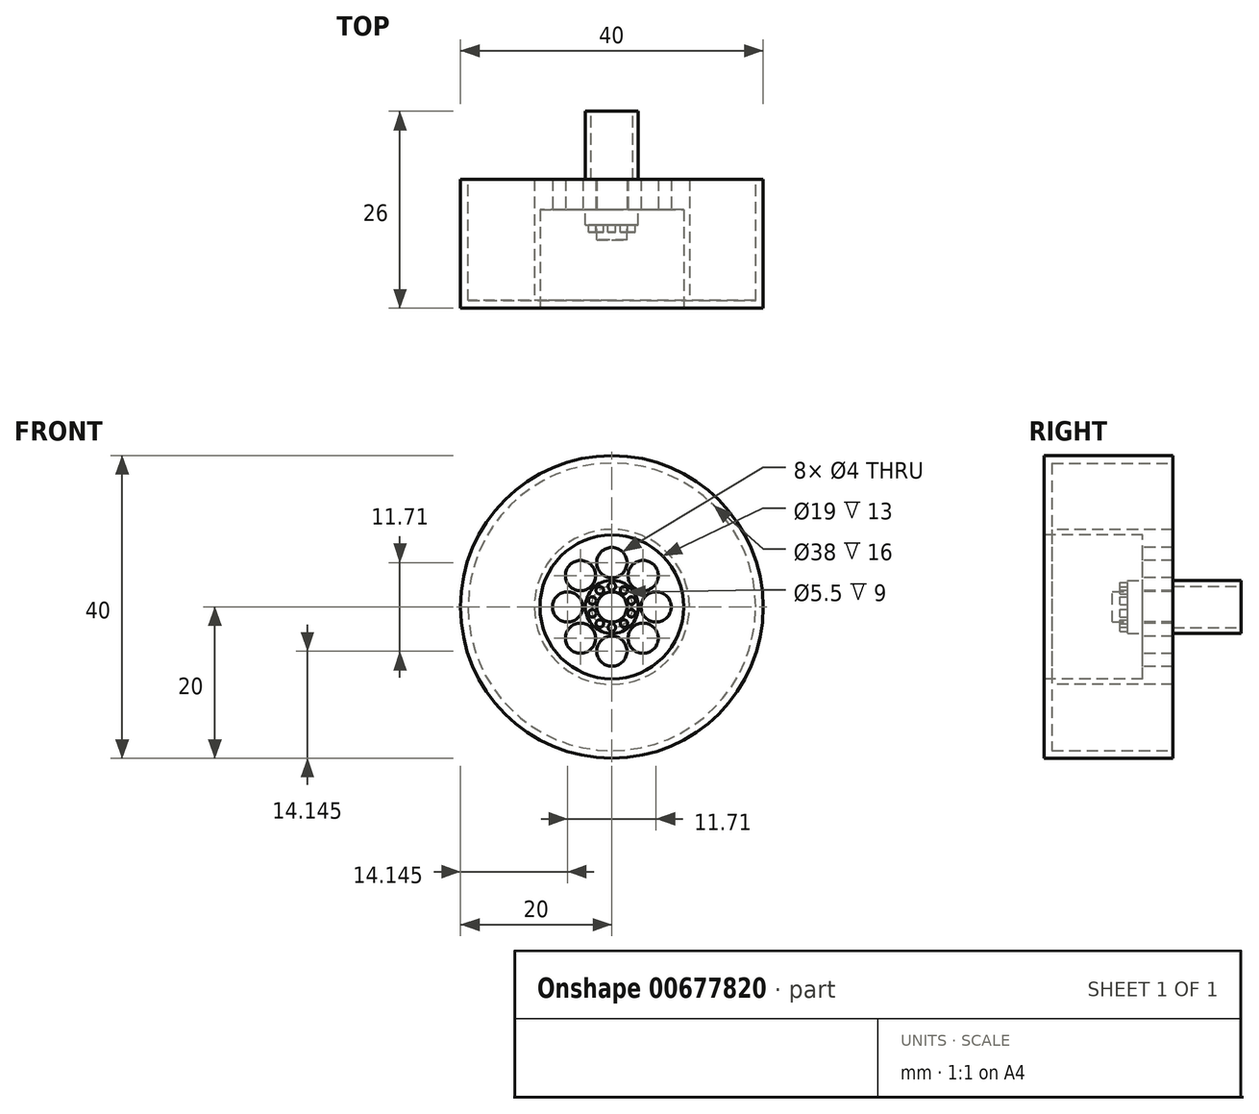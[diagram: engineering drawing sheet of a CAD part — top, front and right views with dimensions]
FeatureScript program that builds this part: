
annotation { "Feature Type Name" : "Feature", "Feature Type Description" : "" }
export const myFeature = defineFeature(function(context is Context, id is Id, definition is map)
    precondition{}
    {
        {
            var Q0;
            Q0=qCreatedBy(makeId("Front.planeOp"),FACE);
            var sketch = newSketch(context, id + "F0", { "sketchPlane" : qUnion([Q0])});
            skCircle(sketch, "E0", {"center": v(0, 0) * mm, "radius": 20 * mm});
            skSolve(sketch);
        }
        {
            var Q0;
            Q0=makeQuery(id+"F0.imprint","IMPRINT",FACE,{"disambiguationData":[TD([[makeQuery(id+"F0.imprint","IMPRINT",EDGE,{"derivedFrom":sQuery(id+"F0.wireOp",EDGE,"E0")}),1.0]])]});
            extrude(context, id + "F1", {"entities" : qUnion([Q0]), "depth" : 17 * mm, "offsetDistance" : 25 * mm});
        }
        {
            var Q0;
            Q0=makeQuery(id+"F1.opExtrude","CAP_FACE",FACE,{"disambiguationData":[OSD([sQuery(id+"F0.wireOp",EDGE,"E0")])],"isStart":false});
            var sketch = newSketch(context, id + "F2", { "sketchPlane" : qUnion([Q0])});
            skCircle(sketch, "E1", {"center": v(0, 0) * mm, "radius": 9.5 * mm});
            skSolve(sketch);
        }
        {
            var Q0;
            Q0=makeQuery(id+"F2.imprint","IMPRINT",FACE,{"disambiguationData":[TD([[makeQuery(id+"F2.imprint","IMPRINT",EDGE,{"derivedFrom":sQuery(id+"F2.wireOp",EDGE,"E1")}),1.0]])]});
            var Q1;
            Q1 = qSketchRegion(id + "F6", true);
            extrude(context, id + "F3", {"entities" : qUnion([Q0, Q1]), "operationType" : NewBodyOperationType.REMOVE, "oppositeDirection" : true, "depth" : 13 * mm, "offsetDistance" : 25 * mm});
        }
        {
            var Q0;
            Q0=makeQuery(id+"F3.boolean.opBoolean","COPY",FACE,{"derivedFrom":makeQuery(id+"F3.opExtrude","CAP_FACE",FACE,{"disambiguationData":[OSD([sQuery(id+"F2.wireOp",EDGE,"E1")])],"isStart":false})});
            var sketch = newSketch(context, id + "F4", { "sketchPlane" : qUnion([Q0])});
            skCircle(sketch, "E2", {"center": v(0, 5.86) * mm, "radius": 2 * mm});
            skCircle(sketch, "E3.1.0", {"center": v(-4.14, 4.14) * mm, "radius": 2 * mm});
            skCircle(sketch, "E3.2.0", {"center": v(-5.86, 0) * mm, "radius": 2 * mm});
            skCircle(sketch, "E3.3.0", {"center": v(-4.14, -4.14) * mm, "radius": 2 * mm});
            skCircle(sketch, "E3.4.0", {"center": v(0, -5.86) * mm, "radius": 2 * mm});
            skCircle(sketch, "E3.5.0", {"center": v(4.14, -4.14) * mm, "radius": 2 * mm});
            skCircle(sketch, "E3.6.0", {"center": v(5.86, 0) * mm, "radius": 2 * mm});
            skCircle(sketch, "E3.7.0", {"center": v(4.14, 4.14) * mm, "radius": 2 * mm});
            skPoint(sketch, "E3.center", {"position": v(0, 0) * mm});
            skSolve(sketch);
        }
        {
            var Q0;
            Q0=makeQuery(id+"F4.imprint","IMPRINT",FACE,{"disambiguationData":[TD([[makeQuery(id+"F4.imprint","IMPRINT",EDGE,{"derivedFrom":sQuery(id+"F4.wireOp",EDGE,"E3.1.0")}),1.0]])]});
            var Q1;
            Q1=makeQuery(id+"F4.imprint","IMPRINT",FACE,{"disambiguationData":[TD([[makeQuery(id+"F4.imprint","IMPRINT",EDGE,{"derivedFrom":sQuery(id+"F4.wireOp",EDGE,"E2")}),1.0]])]});
            var Q2;
            Q2=makeQuery(id+"F4.imprint","IMPRINT",FACE,{"disambiguationData":[TD([[makeQuery(id+"F4.imprint","IMPRINT",EDGE,{"derivedFrom":sQuery(id+"F4.wireOp",EDGE,"E3.7.0")}),1.0]])]});
            var Q3;
            Q3=makeQuery(id+"F4.imprint","IMPRINT",FACE,{"disambiguationData":[TD([[makeQuery(id+"F4.imprint","IMPRINT",EDGE,{"derivedFrom":sQuery(id+"F4.wireOp",EDGE,"E3.6.0")}),1.0]])]});
            var Q4;
            Q4=makeQuery(id+"F4.imprint","IMPRINT",FACE,{"disambiguationData":[TD([[makeQuery(id+"F4.imprint","IMPRINT",EDGE,{"derivedFrom":sQuery(id+"F4.wireOp",EDGE,"E3.5.0")}),1.0]])]});
            var Q5;
            Q5=makeQuery(id+"F4.imprint","IMPRINT",FACE,{"disambiguationData":[TD([[makeQuery(id+"F4.imprint","IMPRINT",EDGE,{"derivedFrom":sQuery(id+"F4.wireOp",EDGE,"E3.4.0")}),1.0]])]});
            var Q6;
            Q6=makeQuery(id+"F4.imprint","IMPRINT",FACE,{"disambiguationData":[TD([[makeQuery(id+"F4.imprint","IMPRINT",EDGE,{"derivedFrom":sQuery(id+"F4.wireOp",EDGE,"E3.3.0")}),1.0]])]});
            var Q7;
            Q7=makeQuery(id+"F4.imprint","IMPRINT",FACE,{"disambiguationData":[TD([[makeQuery(id+"F4.imprint","IMPRINT",EDGE,{"derivedFrom":sQuery(id+"F4.wireOp",EDGE,"E3.2.0")}),1.0]])]});
            extrude(context, id + "F5", {"entities" : qUnion([Q0, Q1, Q2, Q3, Q4, Q5, Q6, Q7]), "operationType" : NewBodyOperationType.REMOVE, "oppositeDirection" : true, "depth" : 4 * mm, "offsetDistance" : 25 * mm});
        }
        {
            var Q0;
            Q0=makeQuery(id+"F3.boolean.opBoolean","COPY",FACE,{"derivedFrom":makeQuery(id+"F3.opExtrude","CAP_FACE",FACE,{"disambiguationData":[OSD([sQuery(id+"F2.wireOp",EDGE,"E1")])],"isStart":false})});
            var sketch = newSketch(context, id + "F6", { "sketchPlane" : qUnion([Q0])});
            skCircle(sketch, "E4", {"center": v(0, 0) * mm, "radius": 3.5 * mm});
            skSolve(sketch);
        }
        {
            var Q0;
            Q0=makeQuery(id+"F6.imprint","IMPRINT",FACE,{"disambiguationData":[TD([[makeQuery(id+"F6.imprint","IMPRINT",EDGE,{"derivedFrom":sQuery(id+"F6.wireOp",EDGE,"E4")}),1.0]])]});
            extrude(context, id + "F7", {"entities" : qUnion([Q0]), "operationType" : NewBodyOperationType.ADD, "depth" : 2 * mm, "offsetDistance" : 25 * mm});
        }
        {
            var Q0;
            Q0=makeQuery(id+"F7.opExtrude","CAP_FACE",FACE,{"disambiguationData":[OSD([sQuery(id+"F6.wireOp",EDGE,"E4")])],"isStart":false});
            var sketch = newSketch(context, id + "F8", { "sketchPlane" : qUnion([Q0])});
            skCircle(sketch, "E5", {"center": v(0, 0) * mm, "radius": 2 * mm});
            skSolve(sketch);
        }
        {
            var Q0;
            Q0=makeQuery(id+"F8.imprint","IMPRINT",FACE,{"disambiguationData":[TD([[makeQuery(id+"F8.imprint","IMPRINT",EDGE,{"derivedFrom":sQuery(id+"F8.wireOp",EDGE,"E5")}),1.0]])]});
            extrude(context, id + "F9", {"entities" : qUnion([Q0]), "operationType" : NewBodyOperationType.ADD, "depth" : 2 * mm, "offsetDistance" : 25 * mm});
        }
        {
            var Q0;
            Q0=makeQuery(id+"F7.opExtrude","CAP_FACE",FACE,{"disambiguationData":[OSD([sQuery(id+"F6.wireOp",EDGE,"E4")])],"isStart":false});
            var sketch = newSketch(context, id + "F10", { "sketchPlane" : qUnion([Q0])});
            skCircle(sketch, "E6", {"center": v(0, 2.71) * mm, "radius": 0.5 * mm});
            skCircle(sketch, "E7.1.0", {"center": v(-1.6, 2.2) * mm, "radius": 0.5 * mm});
            skCircle(sketch, "E7.2.0", {"center": v(-2.58, 0.84) * mm, "radius": 0.5 * mm});
            skCircle(sketch, "E7.3.0", {"center": v(-2.58, -0.84) * mm, "radius": 0.5 * mm});
            skCircle(sketch, "E7.4.0", {"center": v(-1.6, -2.2) * mm, "radius": 0.5 * mm});
            skCircle(sketch, "E7.5.0", {"center": v(0, -2.71) * mm, "radius": 0.5 * mm});
            skCircle(sketch, "E7.6.0", {"center": v(1.6, -2.2) * mm, "radius": 0.5 * mm});
            skCircle(sketch, "E7.7.0", {"center": v(2.58, -0.84) * mm, "radius": 0.5 * mm});
            skCircle(sketch, "E7.8.0", {"center": v(2.58, 0.84) * mm, "radius": 0.5 * mm});
            skCircle(sketch, "E7.9.0", {"center": v(1.6, 2.2) * mm, "radius": 0.5 * mm});
            skPoint(sketch, "E7.center", {"position": v(0, 0) * mm});
            skSolve(sketch);
        }
        {
            var Q0;
            Q0=makeQuery(id+"F10.imprint","IMPRINT",FACE,{"disambiguationData":[TD([[makeQuery(id+"F10.imprint","IMPRINT",EDGE,{"derivedFrom":sQuery(id+"F10.wireOp",EDGE,"E6")}),1.0]])]});
            var Q1;
            Q1=makeQuery(id+"F10.imprint","IMPRINT",FACE,{"disambiguationData":[TD([[makeQuery(id+"F10.imprint","IMPRINT",EDGE,{"derivedFrom":sQuery(id+"F10.wireOp",EDGE,"E7.9.0")}),1.0]])]});
            var Q2;
            Q2=makeQuery(id+"F10.imprint","IMPRINT",FACE,{"disambiguationData":[TD([[makeQuery(id+"F10.imprint","IMPRINT",EDGE,{"derivedFrom":sQuery(id+"F10.wireOp",EDGE,"E7.8.0")}),1.0]])]});
            var Q3;
            Q3=makeQuery(id+"F10.imprint","IMPRINT",FACE,{"disambiguationData":[TD([[makeQuery(id+"F10.imprint","IMPRINT",EDGE,{"derivedFrom":sQuery(id+"F10.wireOp",EDGE,"E7.7.0")}),1.0]])]});
            var Q4;
            Q4=makeQuery(id+"F10.imprint","IMPRINT",FACE,{"disambiguationData":[TD([[makeQuery(id+"F10.imprint","IMPRINT",EDGE,{"derivedFrom":sQuery(id+"F10.wireOp",EDGE,"E7.6.0")}),1.0]])]});
            var Q5;
            Q5=makeQuery(id+"F10.imprint","IMPRINT",FACE,{"disambiguationData":[TD([[makeQuery(id+"F10.imprint","IMPRINT",EDGE,{"derivedFrom":sQuery(id+"F10.wireOp",EDGE,"E7.5.0")}),1.0]])]});
            var Q6;
            Q6=makeQuery(id+"F10.imprint","IMPRINT",FACE,{"disambiguationData":[TD([[makeQuery(id+"F10.imprint","IMPRINT",EDGE,{"derivedFrom":sQuery(id+"F10.wireOp",EDGE,"E7.4.0")}),1.0]])]});
            var Q7;
            Q7=makeQuery(id+"F10.imprint","IMPRINT",FACE,{"disambiguationData":[TD([[makeQuery(id+"F10.imprint","IMPRINT",EDGE,{"derivedFrom":sQuery(id+"F10.wireOp",EDGE,"E7.3.0")}),1.0]])]});
            var Q8;
            Q8=makeQuery(id+"F10.imprint","IMPRINT",FACE,{"disambiguationData":[TD([[makeQuery(id+"F10.imprint","IMPRINT",EDGE,{"derivedFrom":sQuery(id+"F10.wireOp",EDGE,"E7.2.0")}),1.0]])]});
            var Q9;
            Q9=makeQuery(id+"F10.imprint","IMPRINT",FACE,{"disambiguationData":[TD([[makeQuery(id+"F10.imprint","IMPRINT",EDGE,{"derivedFrom":sQuery(id+"F10.wireOp",EDGE,"E7.1.0")}),1.0]])]});
            extrude(context, id + "F11", {"entities" : qUnion([Q0, Q1, Q2, Q3, Q4, Q5, Q6, Q7, Q8, Q9]), "operationType" : NewBodyOperationType.ADD, "depth" : 1 * mm, "offsetDistance" : 25 * mm});
        }
        {
            var Q0;
            Q0=makeQuery(id+"F1.opExtrude","CAP_FACE",FACE,{"disambiguationData":[OSD([sQuery(id+"F0.wireOp",EDGE,"E0")])],"isStart":true});
            var sketch = newSketch(context, id + "F12", { "sketchPlane" : qUnion([Q0])});
            skCircle(sketch, "E8", {"center": v(0, 0) * mm, "radius": 3.5 * mm});
            skSolve(sketch);
        }
        {
            var Q0;
            Q0=makeQuery(id+"F12.imprint","IMPRINT",FACE,{"disambiguationData":[TD([[makeQuery(id+"F12.imprint","IMPRINT",EDGE,{"derivedFrom":sQuery(id+"F12.wireOp",EDGE,"E8")}),1.0]])]});
            extrude(context, id + "F13", {"entities" : qUnion([Q0]), "operationType" : NewBodyOperationType.ADD, "depth" : 9 * mm, "offsetDistance" : 25 * mm});
        }
        {
            var Q0;
            Q0=makeQuery(id+"F13.opExtrude","CAP_FACE",FACE,{"disambiguationData":[OSD([sQuery(id+"F12.wireOp",EDGE,"E8")])],"isStart":false});
            var sketch = newSketch(context, id + "F14", { "sketchPlane" : qUnion([Q0])});
            skCircle(sketch, "E9", {"center": v(0, 0) * mm, "radius": 2.75 * mm});
            skSolve(sketch);
        }
        {
            var Q0;
            Q0 = qSketchRegion(id + "F14", true);
            extrude(context, id + "F15", {"entities" : qUnion([Q0]), "operationType" : NewBodyOperationType.REMOVE, "oppositeDirection" : true, "depth" : 9 * mm, "offsetDistance" : 25 * mm});
        }
        {
            var Q0;
            Q0=makeQuery(id+"F1.opExtrude","CAP_FACE",FACE,{"disambiguationData":[OSD([sQuery(id+"F0.wireOp",EDGE,"E0")])],"isStart":true});
            var sketch = newSketch(context, id + "F16", { "sketchPlane" : qUnion([Q0])});
            skCircle(sketch, "E10", {"center": v(0, 0) * mm, "radius": 9.5 * mm});
            skCircle(sketch, "E11", {"center": v(0, 0) * mm, "radius": 19 * mm});
            skSolve(sketch);
        }
        {
            var Q0;
            Q0=makeQuery(id+"F16.imprint","IMPRINT",FACE,{"disambiguationData":[TD([[makeQuery(id+"F16.imprint","IMPRINT",EDGE,{"derivedFrom":sQuery(id+"F16.wireOp",EDGE,"E10")}),-1.0]])]});
            extrude(context, id + "F17", {"entities" : qUnion([Q0]), "operationType" : NewBodyOperationType.REMOVE, "oppositeDirection" : true, "depth" : 16 * mm, "offsetDistance" : 25 * mm});
        }
        {
            var Q0;
            Q0=makeQuery(id+"F1.opExtrude","CAP_FACE",FACE,{"disambiguationData":[OSD([sQuery(id+"F0.wireOp",EDGE,"E0")])],"isStart":false});
            var sketch = newSketch(context, id + "F18", { "sketchPlane" : qUnion([Q0])});
            skCircle(sketch, "E12", {"center": v(0, 0) * mm, "radius": 10.25 * mm});
            skSolve(sketch);
        }
        {
            var Q0;
            Q0=makeQuery(id+"F18.imprint","IMPRINT",FACE,{"disambiguationData":[TD([[makeQuery(id+"F18.imprint","IMPRINT",EDGE,{"derivedFrom":sQuery(id+"F18.wireOp",EDGE,"E12")}),1.0]])]});
            extrude(context, id + "F19", {"entities" : qUnion([Q0]), "operationType" : NewBodyOperationType.ADD, "oppositeDirection" : true, "depth" : 17 * mm, "offsetDistance" : 25 * mm});
        }
    });
